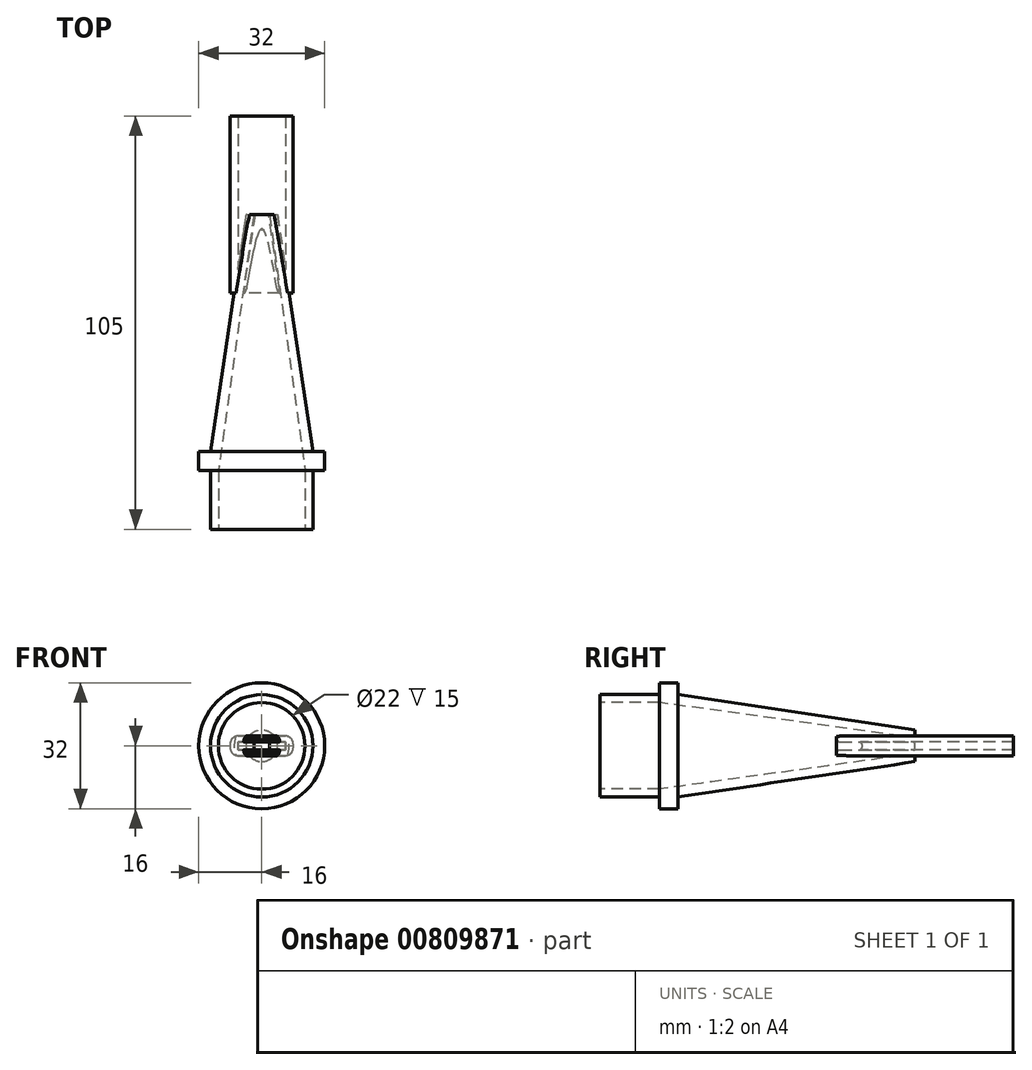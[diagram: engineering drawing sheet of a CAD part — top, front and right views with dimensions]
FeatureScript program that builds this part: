
annotation { "Feature Type Name" : "Feature", "Feature Type Description" : "" }
export const myFeature = defineFeature(function(context is Context, id is Id, definition is map)
    precondition{}
    {
        {
            var Q0;
            Q0=qCreatedBy(makeId("Right.planeOp"),FACE);
            var sketch = newSketch(context, id + "F0", { "sketchPlane" : qUnion([Q0])});
            skLineSegment(sketch, "E0", {"start": v(0, 11) * mm, "end": v(-15, 11) * mm});
            skLineSegment(sketch, "E1", {"start": v(-15, 11) * mm, "end": v(-15, 13) * mm});
            skLineSegment(sketch, "E2", {"start": v(0, 13) * mm, "end": v(0, 16) * mm});
            skLineSegment(sketch, "E3", {"start": v(0, 16) * mm, "end": v(4.72, 16) * mm});
            skLineSegment(sketch, "E4", {"start": v(4.72, 16) * mm, "end": v(4.72, 13) * mm});
            skLineSegment(sketch, "E5", {"start": v(4.72, 13) * mm, "end": v(65, 4) * mm});
            skLineSegment(sketch, "E6", {"start": v(65, 4) * mm, "end": v(65, 2) * mm});
            skLineSegment(sketch, "E7", {"start": v(65, 2) * mm, "end": v(0, 11) * mm});
            skLineSegment(sketch, "E8", {"start": v(0, 13) * mm, "end": v(-15, 13) * mm});
            skLineSegment(sketch, "E9", {"start": v(-35.25, 0) * mm, "end": v(73.84, 0) * mm});
            skSolve(sketch);
        }
        {
            var Q0;
            Q0=makeQuery(id+"F0.imprint","IMPRINT",FACE,{"disambiguationData":[TD([[makeQuery(id+"F0.imprint","IMPRINT",EDGE,{"derivedFrom":sQuery(id+"F0.wireOp",EDGE,"E0")}),-1.0]])]});
            var Q1;
            Q1=sQuery(id+"F0.wireOp",EDGE,"E9");
            revolve(context, id + "F1", {"surfaceOperationType" : NewSurfaceOperationType.NEW, "entities" : qUnion([Q0]), "axis" : qUnion([Q1]), "revolveType" : RevolveType.FULL});
        }
        {
            var Q0;
            Q0=makeQuery(id+"F1.opRevolve","SWEPT_FACE",FACE,{"disambiguationData":[OSD([sQuery(id+"F0.wireOp",EDGE,"E6")])]});
            var sketch = newSketch(context, id + "F2", { "sketchPlane" : qUnion([Q0])});
            skLineSegment(sketch, "E10.bottom", {"start": v(-8, 2.5) * mm, "end": v(8, 2.5) * mm});
            skLineSegment(sketch, "E10.top", {"start": v(-8, -2.5) * mm, "end": v(8, -2.5) * mm});
            skLineSegment(sketch, "E10.left", {"start": v(-8, 2.5) * mm, "end": v(-8, -2.5) * mm});
            skLineSegment(sketch, "E10.right", {"start": v(8, 2.5) * mm, "end": v(8, -2.5) * mm});
            skPoint(sketch, "E10.middle", {"position": v(0, 0) * mm});
            skLineSegment(sketch, "E11.bottom", {"start": v(-6, 1) * mm, "end": v(6, 1) * mm});
            skLineSegment(sketch, "E11.top", {"start": v(-6, -1) * mm, "end": v(6, -1) * mm});
            skLineSegment(sketch, "E11.left", {"start": v(-6, 1) * mm, "end": v(-6, -1) * mm});
            skLineSegment(sketch, "E11.right", {"start": v(6, 1) * mm, "end": v(6, -1) * mm});
            skSolve(sketch);
        }
        {
            var Q0;
            {var subQ0=sQuery(id+"F2.wireOp",EDGE,"E10.left");Q0=makeQuery(id+"F2.imprint","IMPRINT",FACE,{"disambiguationData":[TD([[makeQuery(id+"F2.imprint","IMPRINT",EDGE,{"derivedFrom":subQ0}),1.0]])]});}
            var Q1;
            {var subQ0=sQuery(id+"F2.wireOp",EDGE,"E10.bottom");var subQ1=sQuery(id+"F0.wireOp",EDGE,"E6");var subQ2=makeQuery(id+"F1.opRevolve","SWEPT_EDGE",EDGE,{"disambiguationData":[OSD([sQuery(id+"F0.wireOp",EDGE,"E5"),subQ1])]});var subQ3=makeQuery(id+"F2.imprint","INTERSECT",VERTEX,{"disambiguationData":[OD(0.0)],"derivedFrom":[subQ2,subQ0]});Q1=makeQuery(id+"F2.imprint","IMPRINT",FACE,{"disambiguationData":[TD([[makeQuery(id+"F2.imprint","IMPRINT",EDGE,{"disambiguationData":[TD([[subQ3,-1.0]])],"derivedFrom":subQ0}),-1.0]])]});}
            var Q2;
            {var subQ1=sQuery(id+"F0.wireOp",EDGE,"E6");var subQ4=makeQuery(id+"F1.opRevolve","SWEPT_EDGE",EDGE,{"disambiguationData":[OSD([sQuery(id+"F0.wireOp",EDGE,"E5"),subQ1])]});var subQ6=sQuery(id+"F2.wireOp",EDGE,"E10.top");var subQ7=makeQuery(id+"F2.imprint","INTERSECT",VERTEX,{"disambiguationData":[OD(0.0)],"derivedFrom":[subQ4,subQ6]});Q2=makeQuery(id+"F2.imprint","IMPRINT",FACE,{"disambiguationData":[TD([[makeQuery(id+"F2.imprint","IMPRINT",EDGE,{"disambiguationData":[TD([[subQ7,-1.0]])],"derivedFrom":subQ6}),1.0]])]});}
            var Q3;
            {var subQ0=sQuery(id+"F2.wireOp",EDGE,"E10.right");Q3=makeQuery(id+"F2.imprint","IMPRINT",FACE,{"disambiguationData":[TD([[makeQuery(id+"F2.imprint","IMPRINT",EDGE,{"derivedFrom":subQ0}),-1.0]])]});}
            var Q4;
            {var subQ0=sQuery(id+"F2.wireOp",EDGE,"E11.bottom");var subQ1=makeQuery(id+"F1.opRevolve","SWEPT_EDGE",EDGE,{"disambiguationData":[OSD([sQuery(id+"F0.wireOp",EDGE,"E6"),sQuery(id+"F0.wireOp",EDGE,"E7")])]});var subQ2=makeQuery(id+"F2.imprint","INTERSECT",VERTEX,{"disambiguationData":[OD(0.0)],"derivedFrom":[subQ1,subQ0]});Q4=makeQuery(id+"F2.imprint","IMPRINT",FACE,{"disambiguationData":[TD([[makeQuery(id+"F2.imprint","IMPRINT",EDGE,{"disambiguationData":[TD([[subQ2,-1.0]])],"derivedFrom":subQ0}),1.0]])]});}
            var Q5;
            {var subQ0=sQuery(id+"F2.wireOp",EDGE,"E11.top");var subQ1=makeQuery(id+"F1.opRevolve","SWEPT_EDGE",EDGE,{"disambiguationData":[OSD([sQuery(id+"F0.wireOp",EDGE,"E6"),sQuery(id+"F0.wireOp",EDGE,"E7")])]});var subQ2=makeQuery(id+"F2.imprint","INTERSECT",VERTEX,{"disambiguationData":[OD(0.0)],"derivedFrom":[subQ1,subQ0]});Q5=makeQuery(id+"F2.imprint","IMPRINT",FACE,{"disambiguationData":[TD([[makeQuery(id+"F2.imprint","IMPRINT",EDGE,{"disambiguationData":[TD([[subQ2,-1.0]])],"derivedFrom":subQ0}),-1.0]])]});}
            extrude(context, id + "F3", {"entities" : qUnion([Q0, Q1, Q2, Q3, Q4, Q5]), "operationType" : NewBodyOperationType.ADD, "depth" : 25 * mm, "offsetDistance" : 25 * mm, "hasSecondDirection" : true, "secondDirectionOppositeDirection" : true, "secondDirectionDepth" : 20 * mm});
        }
        {
            var Q0;
            Q0=makeQuery(id+"F3.opExtrude","SWEPT_EDGE",EDGE,{"disambiguationData":[OSD([sQuery(id+"F2.wireOp",EDGE,"E10.bottom"),sQuery(id+"F2.wireOp",EDGE,"E10.left")])]});
            var Q1;
            Q1=makeQuery(id+"F3.opExtrude","SWEPT_EDGE",EDGE,{"disambiguationData":[OSD([sQuery(id+"F2.wireOp",EDGE,"E10.bottom"),sQuery(id+"F2.wireOp",EDGE,"E10.right")])]});
            var Q2;
            Q2=makeQuery(id+"F3.opExtrude","SWEPT_EDGE",EDGE,{"disambiguationData":[OSD([sQuery(id+"F2.wireOp",EDGE,"E10.top"),sQuery(id+"F2.wireOp",EDGE,"E10.right")])]});
            var Q3;
            Q3=makeQuery(id+"F3.opExtrude","SWEPT_EDGE",EDGE,{"disambiguationData":[OSD([sQuery(id+"F2.wireOp",EDGE,"E10.top"),sQuery(id+"F2.wireOp",EDGE,"E10.left")])]});
            fillet(context, id + "F4", {"entities" : qUnion([Q0, Q1, Q2, Q3]), "radius" : 2 * mm, "tangentPropagation" : true, "allowEdgeOverflow" : false});
        }
        {
            var Q0;
            {var subQ0=sQuery(id+"F2.wireOp",EDGE,"E10.bottom");Q0=makeQuery(id+"F3.boolean.opBoolean","SPLIT",EDGE,{"disambiguationData":[TD([makeQuery(id+"F1.opRevolve","SWEPT_FACE",FACE,{"disambiguationData":[OSD([sQuery(id+"F0.wireOp",EDGE,"E7")])]})])],"derivedFrom":makeQuery(id+"F3.opExtrude","CAP_EDGE",EDGE,{"disambiguationData":[OSD([subQ0])],"isStart":true})});}
            var Q1;
            {var subQ0=sQuery(id+"F2.wireOp",EDGE,"E10.top");Q1=makeQuery(id+"F3.boolean.opBoolean","SPLIT",EDGE,{"disambiguationData":[TD([makeQuery(id+"F1.opRevolve","SWEPT_FACE",FACE,{"disambiguationData":[OSD([sQuery(id+"F0.wireOp",EDGE,"E7")])]})])],"derivedFrom":makeQuery(id+"F3.opExtrude","CAP_EDGE",EDGE,{"disambiguationData":[OSD([subQ0])],"isStart":true})});}
            var Q2;
            Q2=makeQuery(id+"F3.opExtrude","CAP_EDGE",EDGE,{"disambiguationData":[OSD([sQuery(id+"F2.wireOp",EDGE,"E11.bottom")])],"isStart":true});
            var Q3;
            Q3=makeQuery(id+"F3.opExtrude","CAP_EDGE",EDGE,{"disambiguationData":[OSD([sQuery(id+"F2.wireOp",EDGE,"E11.top")])],"isStart":true});
            fillet(context, id + "F5", {"entities" : qUnion([Q0, Q1, Q2, Q3]), "radius" : 1 * mm, "tangentPropagation" : true, "allowEdgeOverflow" : false});
        }
    });
